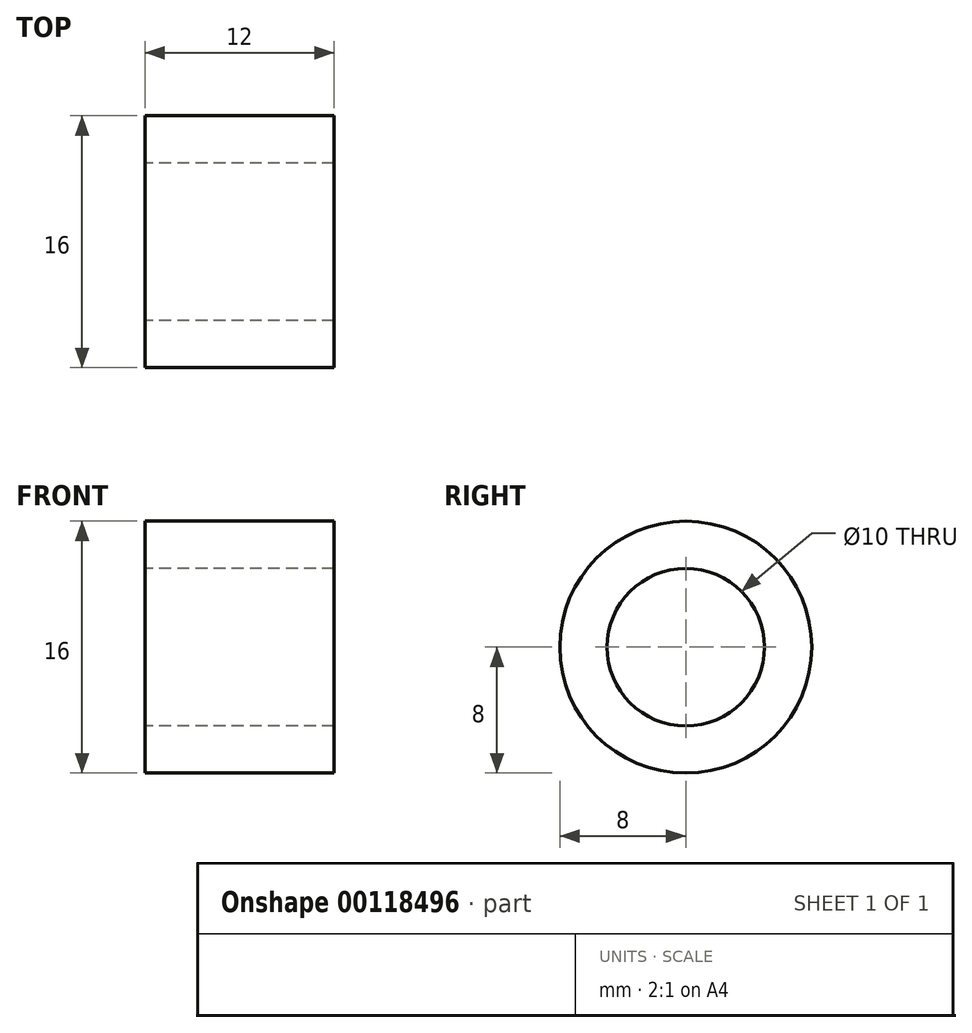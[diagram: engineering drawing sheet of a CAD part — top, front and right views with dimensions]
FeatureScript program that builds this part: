
annotation { "Feature Type Name" : "Feature", "Feature Type Description" : "" }
export const myFeature = defineFeature(function(context is Context, id is Id, definition is map)
    precondition{}
    {
        {
            var Q0;
            Q0=qCreatedBy(makeId("Front.planeOp"),FACE);
            var sketch = newSketch(context, id + "F0", { "sketchPlane" : qUnion([Q0])});
            skLineSegment(sketch, "E0", {"start": v(0, 0) * mm, "end": v(18.25, 0) * mm, "construction": true});
            skLineSegment(sketch, "E1", {"start": v(0, 5) * mm, "end": v(12, 5) * mm});
            skLineSegment(sketch, "E2", {"start": v(12, 5) * mm, "end": v(12, 8) * mm});
            skLineSegment(sketch, "E3", {"start": v(12, 8) * mm, "end": v(0, 8) * mm});
            skLineSegment(sketch, "E4", {"start": v(0, 8) * mm, "end": v(0, 5) * mm});
            skSolve(sketch);
        }
        {
            var Q0;
            Q0=makeQuery(id+"F0.imprint","IMPRINT",FACE,{"disambiguationData":[TD([[makeQuery(id+"F0.imprint","IMPRINT",EDGE,{"derivedFrom":sQuery(id+"F0.wireOp",EDGE,"E1")}),1.0]])]});
            var Q1;
            Q1=sQuery(id+"F0.wireOp",EDGE,"E0");
            revolve(context, id + "F1", {"entities" : qUnion([Q0]), "axis" : qUnion([Q1]), "revolveType" : RevolveType.FULL});
        }
    });
